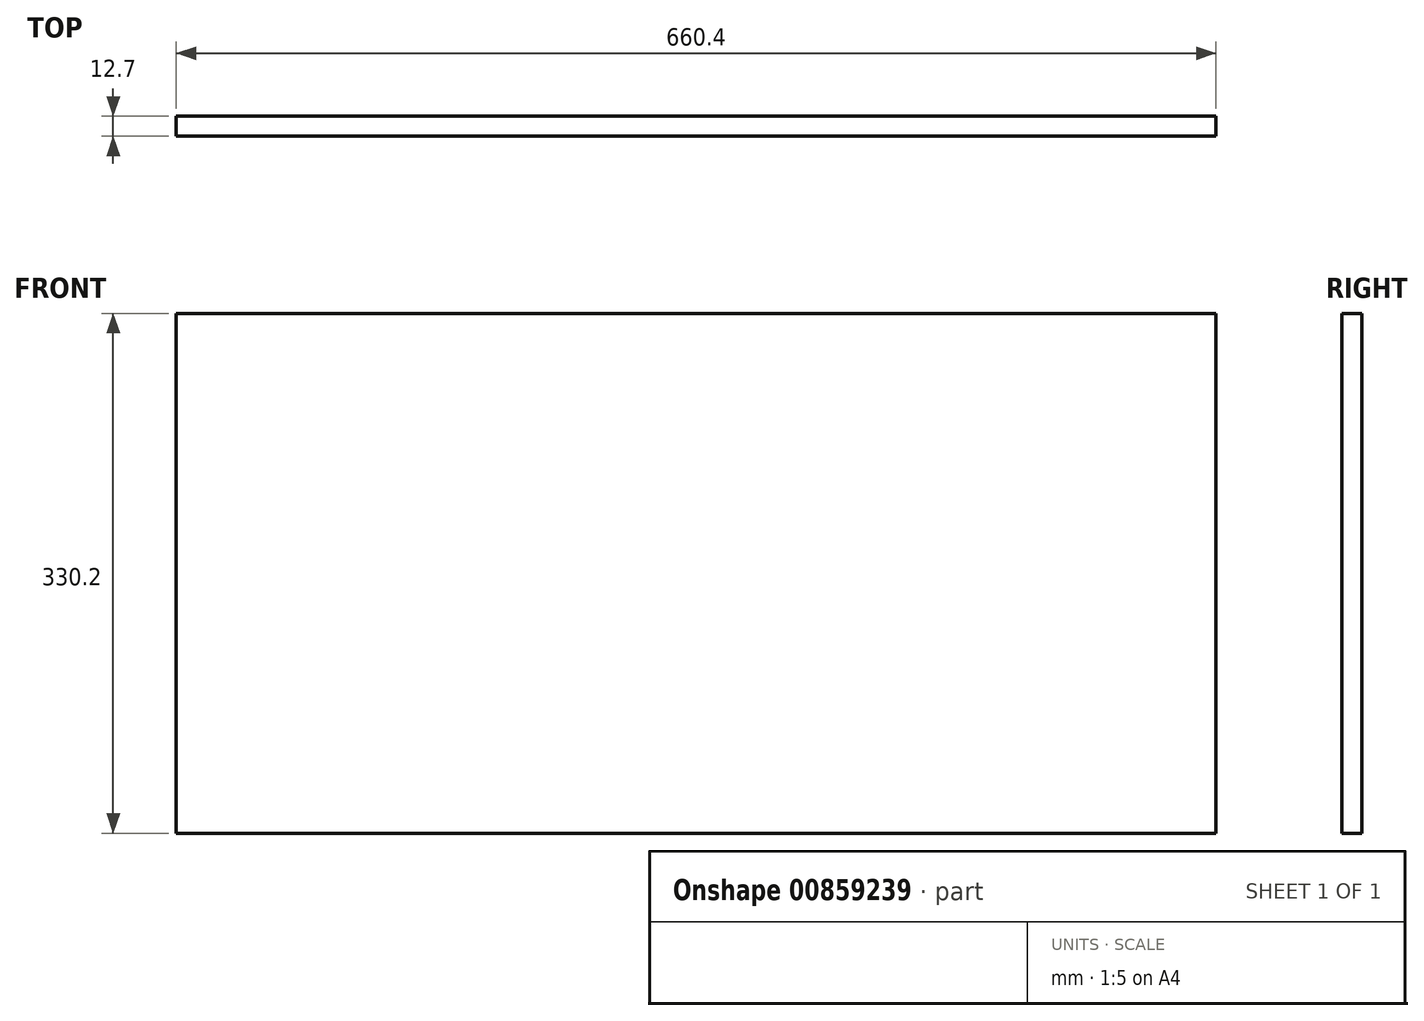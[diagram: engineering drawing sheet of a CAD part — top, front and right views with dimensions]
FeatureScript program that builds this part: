
annotation { "Feature Type Name" : "Feature", "Feature Type Description" : "" }
export const myFeature = defineFeature(function(context is Context, id is Id, definition is map)
    precondition{}
    {
        {
            var Q0;
            Q0=qCreatedBy(makeId("Front.planeOp"),FACE);
            var sketch = newSketch(context, id + "F0", { "sketchPlane" : qUnion([Q0])});
            skLineSegment(sketch, "E0.bottom", {"start": v(0, 0) * mm, "end": v(-660.4, 0) * mm});
            skLineSegment(sketch, "E0.top", {"start": v(0, 330.2) * mm, "end": v(-660.4, 330.2) * mm});
            skLineSegment(sketch, "E0.left", {"start": v(0, 0) * mm, "end": v(0, 330.2) * mm});
            skLineSegment(sketch, "E0.right", {"start": v(-660.4, 0) * mm, "end": v(-660.4, 330.2) * mm});
            skSolve(sketch);
        }
        {
            var Q0;
            Q0=makeQuery(id+"F0.imprint","IMPRINT",FACE,{"disambiguationData":[TD([[makeQuery(id+"F0.imprint","IMPRINT",EDGE,{"derivedFrom":sQuery(id+"F0.wireOp",EDGE,"E0.bottom")}),-1.0]])]});
            extrude(context, id + "F1", {"entities" : qUnion([Q0]), "depth" : 12.7 * mm, "offsetDistance" : 25.4 * mm});
        }
    });
